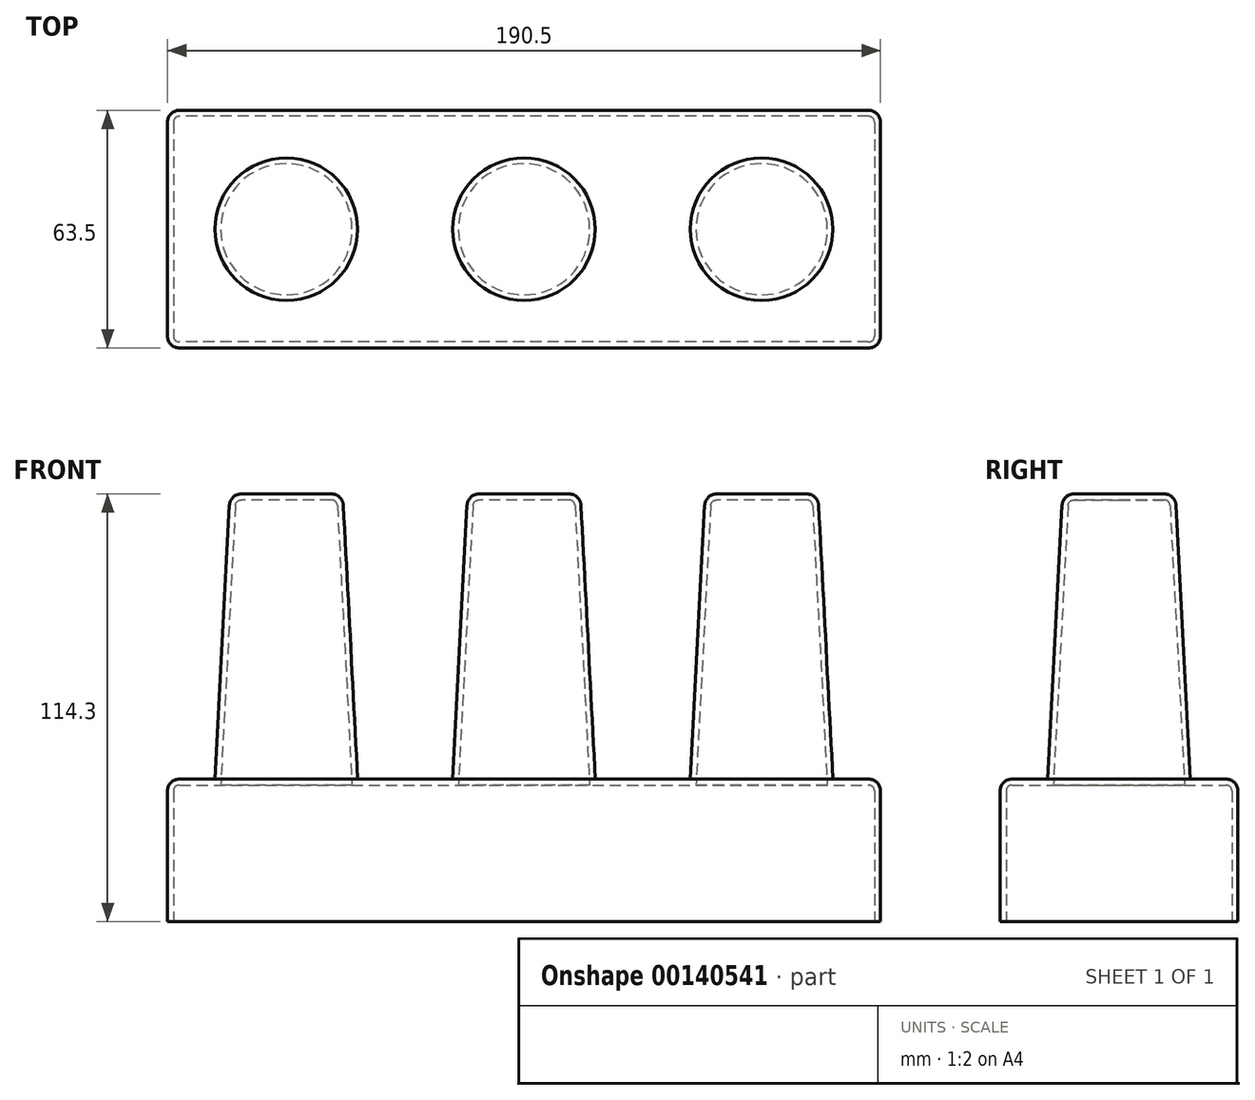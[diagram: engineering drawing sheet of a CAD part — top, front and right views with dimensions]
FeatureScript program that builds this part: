
annotation { "Feature Type Name" : "Feature", "Feature Type Description" : "" }
export const myFeature = defineFeature(function(context is Context, id is Id, definition is map)
    precondition{}
    {
        {
            var Q0;
            Q0=qCreatedBy(makeId("Top.planeOp"),FACE);
            var sketch = newSketch(context, id + "F0", { "sketchPlane" : qUnion([Q0])});
            skLineSegment(sketch, "E0.bottom", {"start": v(95.25, 31.75) * mm, "end": v(-95.25, 31.75) * mm});
            skLineSegment(sketch, "E0.top", {"start": v(95.25, -31.75) * mm, "end": v(-95.25, -31.75) * mm});
            skLineSegment(sketch, "E0.left", {"start": v(95.25, 31.75) * mm, "end": v(95.25, -31.75) * mm});
            skLineSegment(sketch, "E0.right", {"start": v(-95.25, 31.75) * mm, "end": v(-95.25, -31.75) * mm});
            skPoint(sketch, "E0.middle", {"position": v(0, 0) * mm});
            skSolve(sketch);
        }
        {
            var Q0;
            Q0=makeQuery(id+"F0.imprint","IMPRINT",FACE,{"disambiguationData":[TD([[makeQuery(id+"F0.imprint","IMPRINT",EDGE,{"derivedFrom":sQuery(id+"F0.wireOp",EDGE,"E0.bottom")}),1.0]])]});
            extrude(context, id + "F4", {"entities" : qUnion([Q0]), "depth" : 38.1 * mm});
        }
        {
            var Q0;
            Q0=makeQuery(id+"F4.opExtrude","CAP_FACE",FACE,{"disambiguationData":[OSD([sQuery(id+"F0.wireOp",EDGE,"E0.bottom"),sQuery(id+"F0.wireOp",EDGE,"E0.top"),sQuery(id+"F0.wireOp",EDGE,"E0.left"),sQuery(id+"F0.wireOp",EDGE,"E0.right")])],"isStart":false});
            var sketch = newSketch(context, id + "F1", { "sketchPlane" : qUnion([Q0])});
            skCircle(sketch, "E1", {"center": v(-63.5, 0) * mm, "radius": 19.05 * mm});
            skCircle(sketch, "E2", {"center": v(0, 0) * mm, "radius": 19.05 * mm});
            skCircle(sketch, "E3", {"center": v(63.5, 0) * mm, "radius": 19.05 * mm});
            skSolve(sketch);
        }
        {
            var Q0;
            Q0=qSketchRegion(id+"F1",true);
            extrude(context, id + "F2", {"entities" : qUnion([Q0]), "operationType" : NewBodyOperationType.ADD, "depth" : 76.2 * mm, "hasDraft" : true, "draftAngle" : 3 * degree, "draftPullDirection" : true});
        }
        {
            var Q0;
            Q0=makeQuery(id+"F4.opExtrude","SWEPT_EDGE",EDGE,{"disambiguationData":[OSD([sQuery(id+"F0.wireOp",EDGE,"E0.top"),sQuery(id+"F0.wireOp",EDGE,"E0.left")])]});
            var Q1;
            Q1=makeQuery(id+"F4.opExtrude","CAP_EDGE",EDGE,{"disambiguationData":[OSD([sQuery(id+"F0.wireOp",EDGE,"E0.left")])],"isStart":false});
            var Q2;
            Q2=makeQuery(id+"F4.opExtrude","SWEPT_EDGE",EDGE,{"disambiguationData":[OSD([sQuery(id+"F0.wireOp",EDGE,"E0.bottom"),sQuery(id+"F0.wireOp",EDGE,"E0.left")])]});
            var Q3;
            Q3=makeQuery(id+"F4.opExtrude","CAP_EDGE",EDGE,{"disambiguationData":[OSD([sQuery(id+"F0.wireOp",EDGE,"E0.bottom")])],"isStart":false});
            var Q4;
            Q4=makeQuery(id+"F4.opExtrude","SWEPT_EDGE",EDGE,{"disambiguationData":[OSD([sQuery(id+"F0.wireOp",EDGE,"E0.bottom"),sQuery(id+"F0.wireOp",EDGE,"E0.right")])]});
            var Q5;
            Q5=makeQuery(id+"F4.opExtrude","SWEPT_EDGE",EDGE,{"disambiguationData":[OSD([sQuery(id+"F0.wireOp",EDGE,"E0.top"),sQuery(id+"F0.wireOp",EDGE,"E0.right")])]});
            var Q6;
            Q6=makeQuery(id+"F2.opExtrude","CAP_FACE",FACE,{"disambiguationData":[OSD([sQuery(id+"F1.wireOp",EDGE,"E1")])],"isStart":false});
            var Q7;
            Q7=makeQuery(id+"F2.opExtrude","CAP_FACE",FACE,{"disambiguationData":[OSD([sQuery(id+"F1.wireOp",EDGE,"E2")])],"isStart":false});
            var Q8;
            Q8=makeQuery(id+"F2.opExtrude","CAP_FACE",FACE,{"disambiguationData":[OSD([sQuery(id+"F1.wireOp",EDGE,"E3")])],"isStart":false});
            var Q9;
            Q9=makeQuery(id+"F4.opExtrude","CAP_EDGE",EDGE,{"disambiguationData":[OSD([sQuery(id+"F0.wireOp",EDGE,"E0.right")])],"isStart":false});
            var Q10;
            Q10=makeQuery(id+"F2.opExtrude","CAP_EDGE",EDGE,{"disambiguationData":[OSD([sQuery(id+"F1.wireOp",EDGE,"E3")])],"isStart":true});
            var Q11;
            Q11=makeQuery(id+"F2.opExtrude","CAP_EDGE",EDGE,{"disambiguationData":[OSD([sQuery(id+"F1.wireOp",EDGE,"E2")])],"isStart":true});
            var Q12;
            Q12=makeQuery(id+"F4.opExtrude","CAP_EDGE",EDGE,{"disambiguationData":[OSD([sQuery(id+"F0.wireOp",EDGE,"E0.top")])],"isStart":false});
            var Q13;
            Q13=makeQuery(id+"F2.opExtrude","CAP_EDGE",EDGE,{"disambiguationData":[OSD([sQuery(id+"F1.wireOp",EDGE,"E1")])],"isStart":true});
            fillet(context, id + "F3", {"entities" : qUnion([Q0, Q1, Q2, Q3, Q4, Q5, Q6, Q7, Q8, Q9, Q10, Q11, Q12, Q13]), "radius" : 3.17 * mm, "tangentPropagation" : true, "allowEdgeOverflow" : false});
        }
        {
            var Q0;
            Q0=makeQuery(id+"F4.opExtrude","CAP_FACE",FACE,{"disambiguationData":[OSD([sQuery(id+"F0.wireOp",EDGE,"E0.bottom"),sQuery(id+"F0.wireOp",EDGE,"E0.top"),sQuery(id+"F0.wireOp",EDGE,"E0.left"),sQuery(id+"F0.wireOp",EDGE,"E0.right")])],"isStart":true});
            shell(context, id + "F5", {"entities" : qUnion([Q0]), "thickness" : 1.59 * mm});
        }
    });
